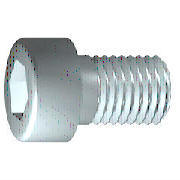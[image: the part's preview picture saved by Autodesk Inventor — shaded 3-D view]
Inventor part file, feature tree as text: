
AUTODESK INVENTOR PART (.ipt)
format: ipt  version: 2022 (Build 260153000, 153)  size: 197,120 bytes
history: native  units: mm (DEFAULTED — no unit token found)
features: sketch x2, other x1, extrude x1, plane x1, fillet x1
ambient origin geometry x7: Origin, YZ Plane, XY Plane, X Axis, Y Axis, Z Axis, Center Point
bodies: Solid1 (feature_tree)
feature tree (6):
  other  "Базовый элемент"
  extrude  "Паз"  Depth=4.65mm
  plane  "Work Plane1"
  fillet  "Fillet2"  Radius=0.276153mm
  sketch  "Эскиз1"
  sketch  "Эскиз2"
